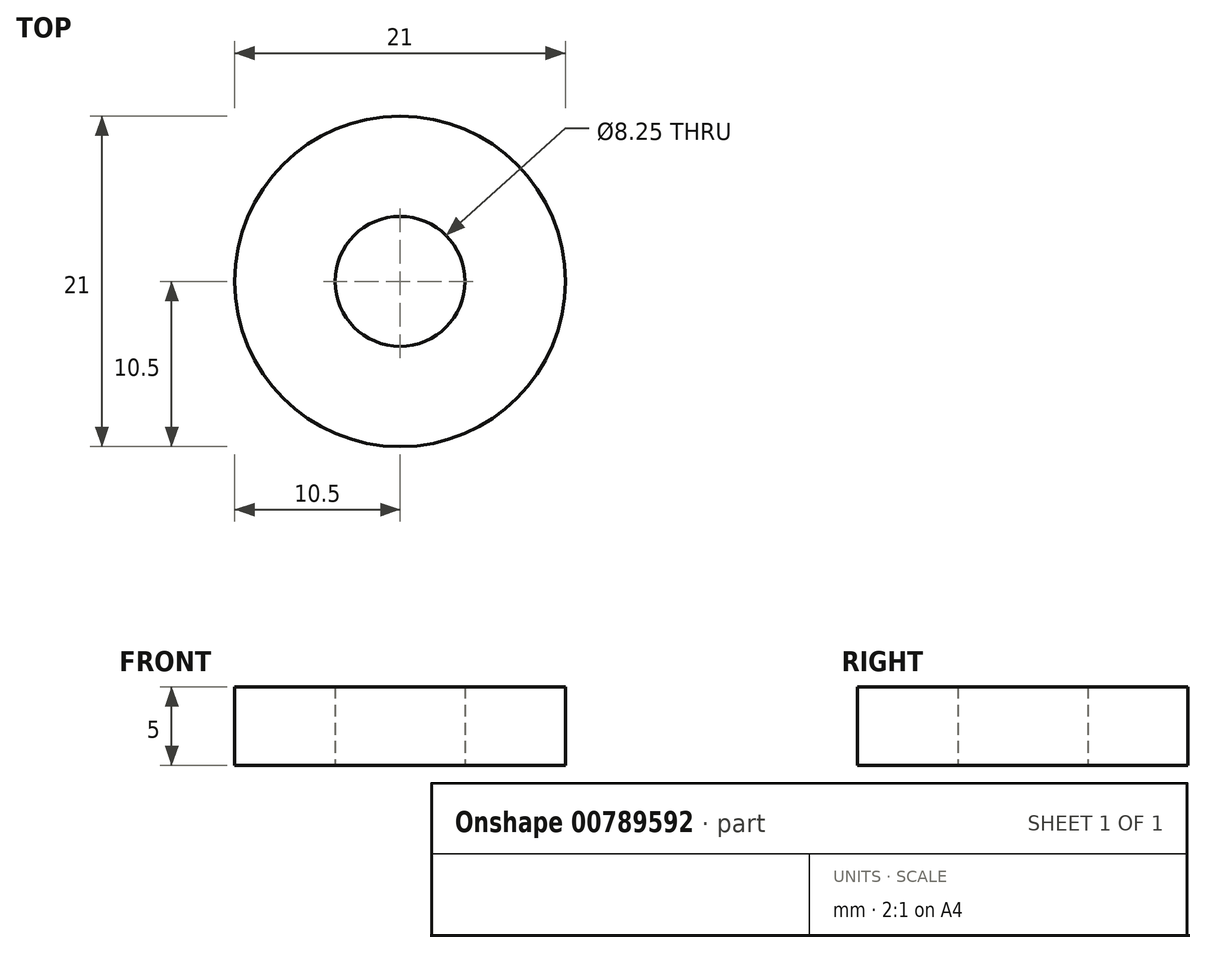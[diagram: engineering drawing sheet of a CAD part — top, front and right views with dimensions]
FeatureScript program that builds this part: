
annotation { "Feature Type Name" : "Feature", "Feature Type Description" : "" }
export const myFeature = defineFeature(function(context is Context, id is Id, definition is map)
    precondition{}
    {
        {
            var Q0;
            Q0=qCreatedBy(makeId("Front.planeOp"),FACE);
            var sketch = newSketch(context, id + "F0", { "sketchPlane" : qUnion([Q0])});
            skLineSegment(sketch, "E0.bottom", {"start": v(-4.12, 0) * mm, "end": v(-10.5, 0) * mm});
            skLineSegment(sketch, "E0.top", {"start": v(-4.12, 5) * mm, "end": v(-10.5, 5) * mm});
            skLineSegment(sketch, "E0.left", {"start": v(-4.12, 0) * mm, "end": v(-4.12, 5) * mm});
            skLineSegment(sketch, "E0.right", {"start": v(-10.5, 0) * mm, "end": v(-10.5, 5) * mm});
            skLineSegment(sketch, "E1", {"start": v(0, 0) * mm, "end": v(0, 17.24) * mm, "construction": true});
            skSolve(sketch);
        }
        {
            var Q0;
            Q0=makeQuery(id+"F0.imprint","IMPRINT",FACE,{"disambiguationData":[TD([[makeQuery(id+"F0.imprint","IMPRINT",EDGE,{"derivedFrom":sQuery(id+"F0.wireOp",EDGE,"E0.bottom")}),-1.0]])]});
            var Q1;
            Q1=sQuery(id+"F0.wireOp",EDGE,"E1");
            revolve(context, id + "F1", {"surfaceOperationType" : NewSurfaceOperationType.NEW, "entities" : qUnion([Q0]), "axis" : qUnion([Q1]), "revolveType" : RevolveType.FULL});
        }
    });
